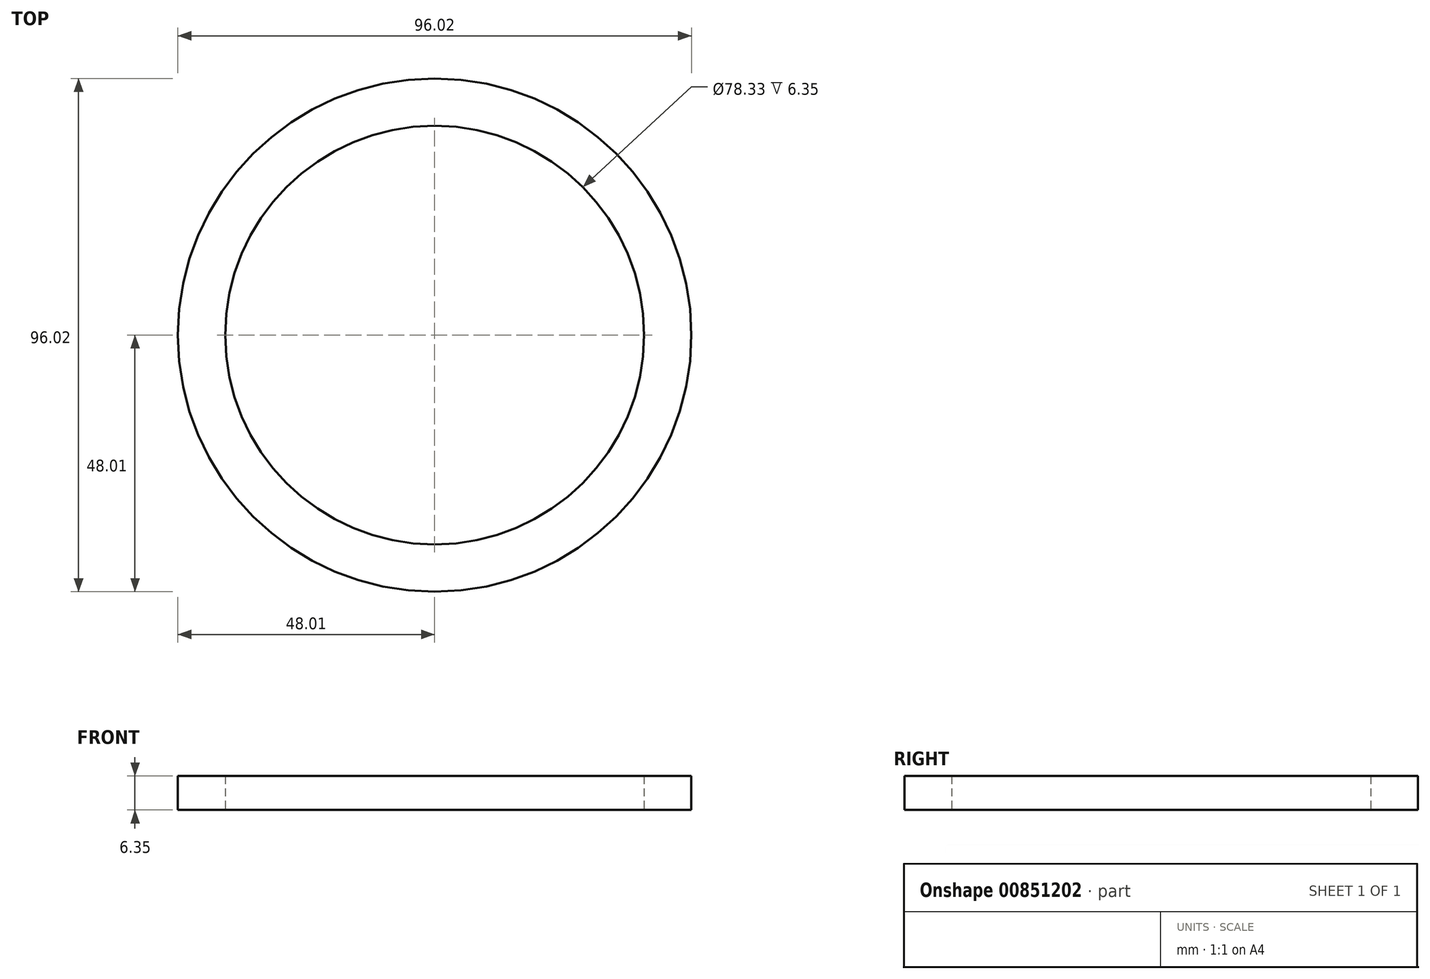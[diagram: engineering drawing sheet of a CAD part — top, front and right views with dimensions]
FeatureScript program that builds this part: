
annotation { "Feature Type Name" : "Feature", "Feature Type Description" : "" }
export const myFeature = defineFeature(function(context is Context, id is Id, definition is map)
    precondition{}
    {
        {
            var Q0;
            Q0=qCreatedBy(makeId("Top.planeOp"),FACE);
            var sketch = newSketch(context, id + "F0", { "sketchPlane" : qUnion([Q0])});
            skCircle(sketch, "E0", {"center": v(0, 0) * mm, "radius": 48 * mm});
            skCircle(sketch, "E1", {"center": v(0, 0) * mm, "radius": 39.17 * mm});
            skSolve(sketch);
        }
        {
            var Q0;
            Q0 = qSketchRegion(id + "F0", true);
            extrude(context, id + "F1", {"entities" : qUnion([Q0]), "depth" : 6.35 * mm, "offsetDistance" : 25.4 * mm});
        }
    });
